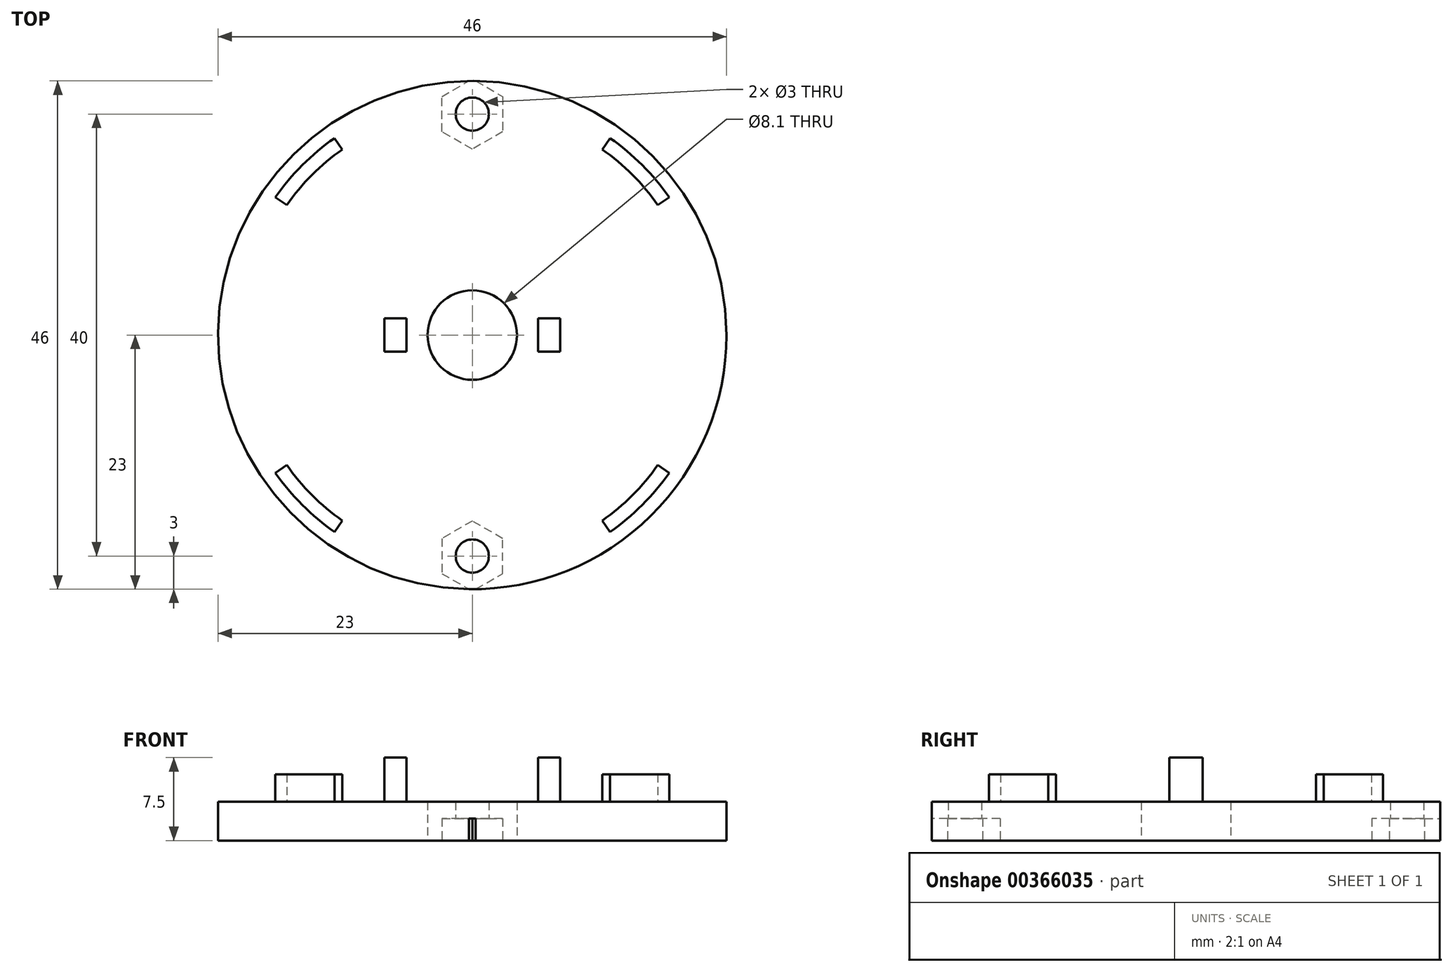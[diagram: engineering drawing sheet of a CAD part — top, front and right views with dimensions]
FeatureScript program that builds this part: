
annotation { "Feature Type Name" : "Feature", "Feature Type Description" : "" }
export const myFeature = defineFeature(function(context is Context, id is Id, definition is map)
    precondition{}
    {
        {
            var Q0;
            Q0=qCreatedBy(makeId("Top.planeOp"),FACE);
            var sketch = newSketch(context, id + "F0", { "sketchPlane" : qUnion([Q0])});
            skCircle(sketch, "E0", {"center": v(0, 0) * mm, "radius": 23 * mm});
            skCircle(sketch, "E1", {"center": v(0, 0) * mm, "radius": 4.05 * mm});
            skSolve(sketch);
        }
        {
            var Q0;
            Q0=makeQuery(id+"F0.imprint","IMPRINT",FACE,{"disambiguationData":[TD([[makeQuery(id+"F0.imprint","IMPRINT",EDGE,{"derivedFrom":sQuery(id+"F0.wireOp",EDGE,"E0")}),1.0]])]});
            extrude(context, id + "F1", {"entities" : qUnion([Q0]), "depth" : 3.5 * mm});
        }
        {
            var Q0;
            Q0=makeQuery(id+"F1.opExtrude","CAP_FACE",FACE,{"disambiguationData":[OSD([sQuery(id+"F0.wireOp",EDGE,"E0"),sQuery(id+"F0.wireOp",EDGE,"E1")])],"isStart":false});
            var sketch = newSketch(context, id + "F2", { "sketchPlane" : qUnion([Q0])});
            skArc(sketch, "E2", {"start": v(17.82, 12.48) * mm, "mid": v(15.38, 15.38) * mm, "end": v(12.48, 17.82) * mm});
            skArc(sketch, "E3", {"start": v(16.8, 11.76) * mm, "mid": v(14.5, 14.5) * mm, "end": v(11.76, 16.8) * mm});
            skLineSegment(sketch, "E4", {"start": v(0, 0) * mm, "end": v(23.4, 33.43) * mm, "construction": true});
            skLineSegment(sketch, "E5", {"start": v(0, 0) * mm, "end": v(36.03, 25.23) * mm, "construction": true});
            skPoint(sketch, "E6", {"position": v(16.8, 11.76) * mm});
            skPoint(sketch, "E7", {"position": v(11.76, 16.8) * mm});
            skPoint(sketch, "E8", {"position": v(17.82, 12.48) * mm});
            skPoint(sketch, "E9", {"position": v(12.48, 17.82) * mm});
            skLineSegment(sketch, "E10", {"start": v(16.8, 11.76) * mm, "end": v(17.82, 12.48) * mm});
            skLineSegment(sketch, "E11", {"start": v(11.76, 16.8) * mm, "end": v(12.48, 17.82) * mm});
            skArc(sketch, "E12.1.0", {"start": v(-11.76, 16.8) * mm, "mid": v(-14.5, 14.5) * mm, "end": v(-16.8, 11.76) * mm});
            skArc(sketch, "E12.1.1", {"start": v(-12.48, 17.82) * mm, "mid": v(-15.38, 15.38) * mm, "end": v(-17.82, 12.48) * mm});
            skArc(sketch, "E12.2.0", {"start": v(-16.8, -11.76) * mm, "mid": v(-14.5, -14.5) * mm, "end": v(-11.76, -16.8) * mm});
            skArc(sketch, "E12.2.1", {"start": v(-17.82, -12.48) * mm, "mid": v(-15.38, -15.38) * mm, "end": v(-12.48, -17.82) * mm});
            skArc(sketch, "E12.3.0", {"start": v(11.76, -16.8) * mm, "mid": v(14.5, -14.5) * mm, "end": v(16.8, -11.76) * mm});
            skArc(sketch, "E12.3.1", {"start": v(12.48, -17.82) * mm, "mid": v(15.38, -15.38) * mm, "end": v(17.82, -12.48) * mm});
            skLineSegment(sketch, "E13", {"start": v(17.82, -12.48) * mm, "end": v(16.8, -11.76) * mm});
            skLineSegment(sketch, "E14", {"start": v(12.48, -17.82) * mm, "end": v(11.76, -16.8) * mm});
            skLineSegment(sketch, "E15", {"start": v(-12.48, -17.82) * mm, "end": v(-11.76, -16.8) * mm});
            skLineSegment(sketch, "E16", {"start": v(-17.82, -12.48) * mm, "end": v(-16.8, -11.76) * mm});
            skLineSegment(sketch, "E17", {"start": v(-16.8, 11.76) * mm, "end": v(-17.82, 12.48) * mm});
            skLineSegment(sketch, "E18", {"start": v(-11.76, 16.8) * mm, "end": v(-12.48, 17.82) * mm});
            skSolve(sketch);
        }
        {
            var Q0;
            Q0 = qSketchRegion(id + "F2", true);
            extrude(context, id + "F3", {"entities" : qUnion([Q0]), "operationType" : NewBodyOperationType.ADD, "depth" : 2.5 * mm});
        }
        {
            var Q0;
            Q0=makeQuery(id+"F1.opExtrude","CAP_FACE",FACE,{"disambiguationData":[OSD([sQuery(id+"F0.wireOp",EDGE,"E0"),sQuery(id+"F0.wireOp",EDGE,"E1")])],"isStart":false});
            var sketch = newSketch(context, id + "F4", { "sketchPlane" : qUnion([Q0])});
            skLineSegment(sketch, "E19.bottom", {"start": v(5.95, 1.5) * mm, "end": v(7.95, 1.5) * mm});
            skLineSegment(sketch, "E19.top", {"start": v(5.95, -1.5) * mm, "end": v(7.95, -1.5) * mm});
            skLineSegment(sketch, "E19.left", {"start": v(5.95, 1.5) * mm, "end": v(5.95, -1.5) * mm});
            skLineSegment(sketch, "E19.right", {"start": v(7.95, 1.5) * mm, "end": v(7.95, -1.5) * mm});
            skLineSegment(sketch, "E20.MirrorCS", {"start": v(-5.95, 1.5) * mm, "end": v(-7.95, 1.5) * mm});
            skLineSegment(sketch, "E21.MirrorCS", {"start": v(-5.95, 1.5) * mm, "end": v(-5.95, -1.5) * mm});
            skLineSegment(sketch, "E22.MirrorCS", {"start": v(-5.95, -1.5) * mm, "end": v(-7.95, -1.5) * mm});
            skLineSegment(sketch, "E23.MirrorCS", {"start": v(-7.95, 1.5) * mm, "end": v(-7.95, -1.5) * mm});
            skSolve(sketch);
        }
        {
            var Q0;
            Q0 = qSketchRegion(id + "F4", true);
            extrude(context, id + "F5", {"entities" : qUnion([Q0]), "operationType" : NewBodyOperationType.ADD, "depth" : 4 * mm});
        }
        {
            var Q0;
            Q0=makeQuery(id+"F1.opExtrude","CAP_FACE",FACE,{"disambiguationData":[OSD([sQuery(id+"F0.wireOp",EDGE,"E0"),sQuery(id+"F0.wireOp",EDGE,"E1")])],"isStart":true});
            var sketch = newSketch(context, id + "F6", { "sketchPlane" : qUnion([Q0])});
            skCircle(sketch, "E24", {"center": v(0, 20) * mm, "radius": 1.5 * mm});
            skCircle(sketch, "E25.MirrorC", {"center": v(0, -20) * mm, "radius": 1.5 * mm});
            skSolve(sketch);
        }
        {
            var Q0;
            Q0 = qSketchRegion(id + "F6", true);
            extrude(context, id + "F7", {"entities" : qUnion([Q0]), "operationType" : NewBodyOperationType.REMOVE, "oppositeDirection" : true, "depth" : 25 * mm});
        }
        {
            var Q0;
            Q0=makeQuery(id+"F1.opExtrude","CAP_FACE",FACE,{"disambiguationData":[OSD([sQuery(id+"F0.wireOp",EDGE,"E0"),sQuery(id+"F0.wireOp",EDGE,"E1")])],"isStart":true});
            var sketch = newSketch(context, id + "F8", { "sketchPlane" : qUnion([Q0])});
            skCircle(sketch, "E26.cCircle", {"center": v(0, 20) * mm, "radius": 2.75 * mm, "construction": true});
            skLineSegment(sketch, "E26.0", {"start": v(-2.75, 18.41) * mm, "end": v(-2.75, 21.59) * mm});
            skLineSegment(sketch, "E26.1", {"start": v(-2.75, 21.59) * mm, "end": v(0, 23.18) * mm});
            skLineSegment(sketch, "E26.2", {"start": v(0, 23.18) * mm, "end": v(2.75, 21.59) * mm});
            skLineSegment(sketch, "E26.3", {"start": v(2.75, 21.59) * mm, "end": v(2.75, 18.41) * mm});
            skLineSegment(sketch, "E26.4", {"start": v(2.75, 18.41) * mm, "end": v(0, 16.82) * mm});
            skLineSegment(sketch, "E26.5", {"start": v(0, 16.82) * mm, "end": v(-2.75, 18.41) * mm});
            skPoint(sketch, "E26.0.midPoint", {"position": v(-2.75, 20) * mm});
            skCircle(sketch, "E27.MirrorC", {"center": v(0, -20) * mm, "radius": 2.75 * mm, "construction": true});
            skLineSegment(sketch, "E28.MirrorCS", {"start": v(2.75, -18.41) * mm, "end": v(0, -16.82) * mm});
            skLineSegment(sketch, "E29.MirrorCS", {"start": v(2.75, -21.59) * mm, "end": v(2.75, -18.41) * mm});
            skLineSegment(sketch, "E30.MirrorCS", {"start": v(0, -23.18) * mm, "end": v(2.75, -21.59) * mm});
            skLineSegment(sketch, "E31.MirrorCS", {"start": v(-2.75, -21.59) * mm, "end": v(0, -23.18) * mm});
            skLineSegment(sketch, "E32.MirrorCS", {"start": v(-2.75, -18.41) * mm, "end": v(-2.75, -21.59) * mm});
            skLineSegment(sketch, "E33.MirrorCS", {"start": v(0, -16.82) * mm, "end": v(-2.75, -18.41) * mm});
            skSolve(sketch);
        }
        {
            var Q0;
            Q0 = qSketchRegion(id + "F8", true);
            extrude(context, id + "F9", {"entities" : qUnion([Q0]), "operationType" : NewBodyOperationType.REMOVE, "oppositeDirection" : true, "depth" : 2 * mm});
        }
    });
